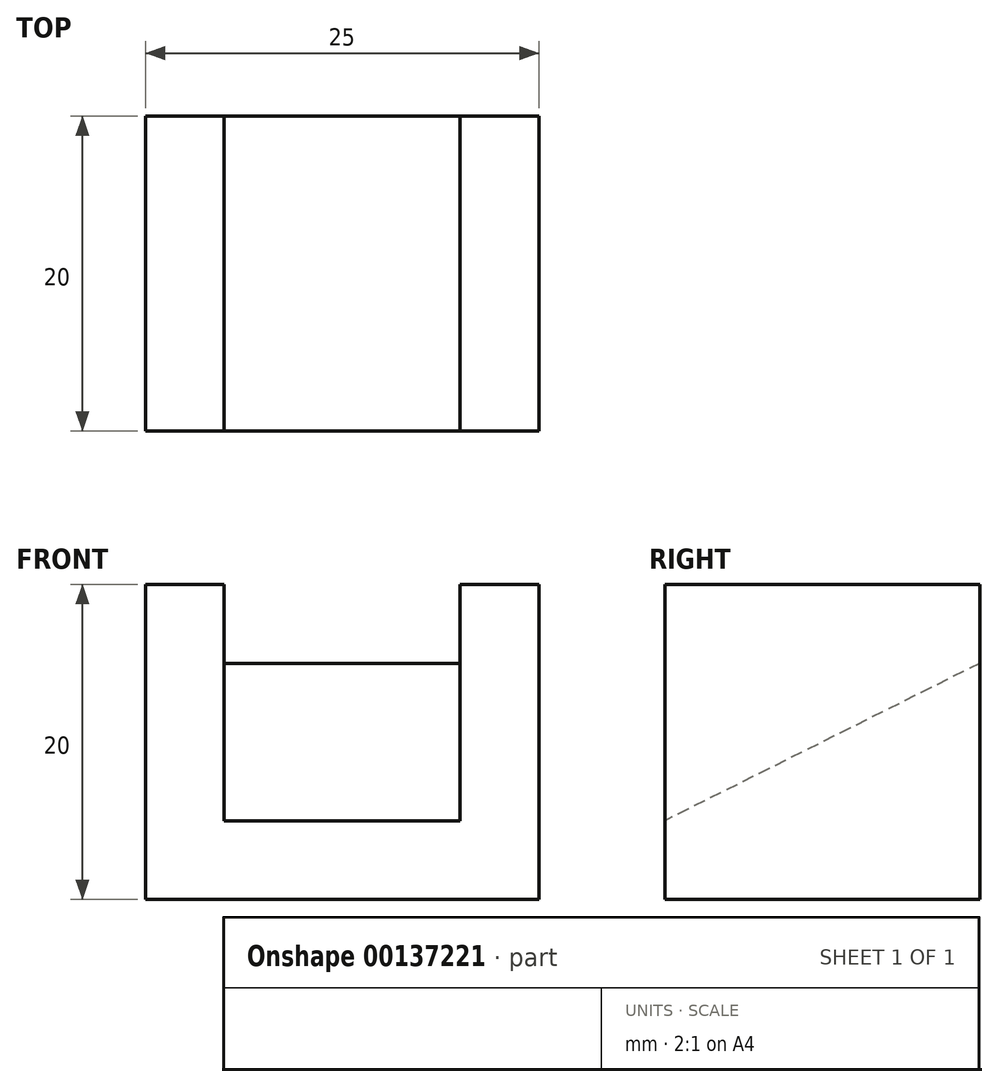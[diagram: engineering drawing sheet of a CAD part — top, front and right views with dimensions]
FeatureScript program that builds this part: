
annotation { "Feature Type Name" : "Feature", "Feature Type Description" : "" }
export const myFeature = defineFeature(function(context is Context, id is Id, definition is map)
    precondition{}
    {
        {
            var Q0;
            Q0=qCreatedBy(makeId("Right.planeOp"),FACE);
            var sketch = newSketch(context, id + "F0", { "sketchPlane" : qUnion([Q0])});
            skLineSegment(sketch, "E0", {"start": v(0, 5) * mm, "end": v(0, 0) * mm});
            skLineSegment(sketch, "E1", {"start": v(0, 0) * mm, "end": v(20, 0) * mm});
            skLineSegment(sketch, "E2", {"start": v(20, 0) * mm, "end": v(20, 15) * mm});
            skLineSegment(sketch, "E3", {"start": v(20, 15) * mm, "end": v(0, 5) * mm});
            skSolve(sketch);
        }
        {
            var Q0;
            Q0 = qSketchRegion(id + "F0", true);
            extrude(context, id + "F1", {"entities" : qUnion([Q0]), "depth" : 20 * mm});
        }
        {
            var Q0;
            Q0=qCreatedBy(makeId("Right.planeOp"),FACE);
            var sketch = newSketch(context, id + "F2", { "sketchPlane" : qUnion([Q0])});
            skLineSegment(sketch, "E4.bottom", {"start": v(0, 0) * mm, "end": v(0, 0) * mm});
            skLineSegment(sketch, "E5.bottom", {"start": v(0, 0) * mm, "end": v(20, 0) * mm});
            skLineSegment(sketch, "E5.top", {"start": v(0, 20) * mm, "end": v(20, 20) * mm});
            skLineSegment(sketch, "E5.left", {"start": v(0, 0) * mm, "end": v(0, 20) * mm});
            skLineSegment(sketch, "E5.right", {"start": v(20, 0) * mm, "end": v(20, 20) * mm});
            skSolve(sketch);
        }
        {
            var Q0;
            Q0 = qSketchRegion(id + "F2", true);
            extrude(context, id + "F3", {"entities" : qUnion([Q0]), "operationType" : NewBodyOperationType.ADD, "depth" : 5 * mm});
        }
        {
            var Q0;
            Q0=makeQuery(id+"F1.opExtrude","CAP_FACE",FACE,{"disambiguationData":[OSD([sQuery(id+"F0.wireOp",EDGE,"E0"),sQuery(id+"F0.wireOp",EDGE,"E1"),sQuery(id+"F0.wireOp",EDGE,"E2"),sQuery(id+"F0.wireOp",EDGE,"E3")])],"isStart":false});
            var sketch = newSketch(context, id + "F4", { "sketchPlane" : qUnion([Q0])});
            skLineSegment(sketch, "E6.bottom", {"start": v(0, 0) * mm, "end": v(20, 0) * mm});
            skLineSegment(sketch, "E6.top", {"start": v(0, 20) * mm, "end": v(20, 20) * mm});
            skLineSegment(sketch, "E6.left", {"start": v(0, 0) * mm, "end": v(0, 20) * mm});
            skLineSegment(sketch, "E6.right", {"start": v(20, 0) * mm, "end": v(20, 20) * mm});
            skSolve(sketch);
        }
        {
            var Q0;
            Q0 = qSketchRegion(id + "F4", true);
            extrude(context, id + "F5", {"entities" : qUnion([Q0]), "operationType" : NewBodyOperationType.ADD, "depth" : 5 * mm});
        }
    });
